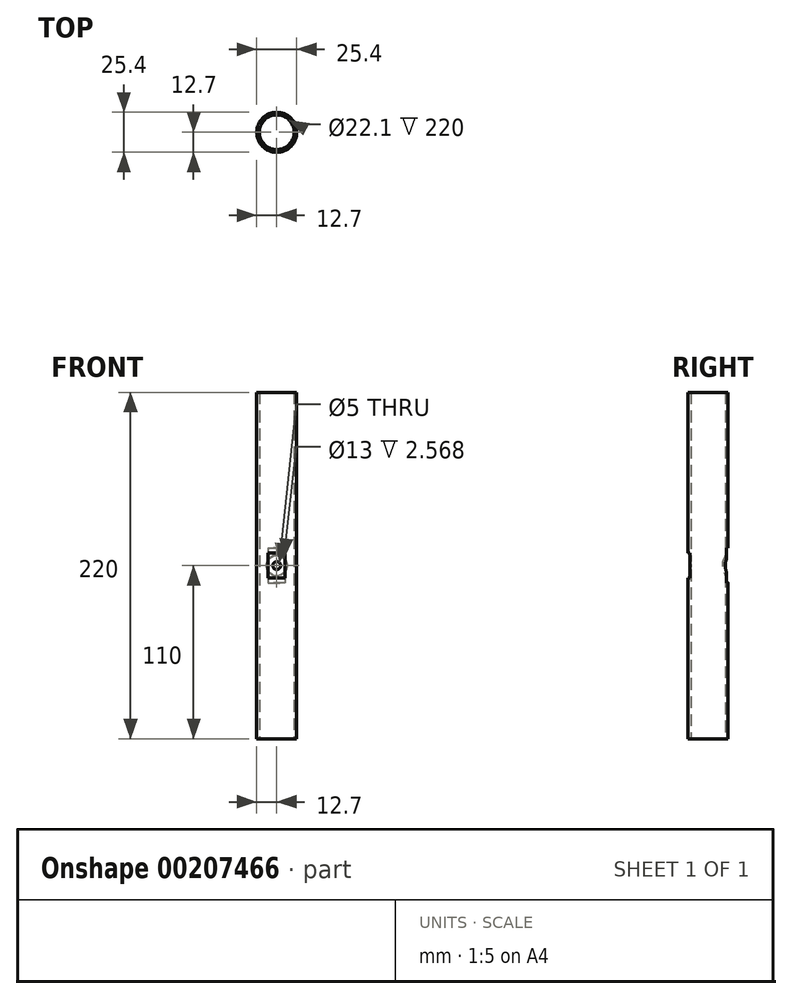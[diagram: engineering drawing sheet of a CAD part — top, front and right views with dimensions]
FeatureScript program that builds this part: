
annotation { "Feature Type Name" : "Feature", "Feature Type Description" : "" }
export const myFeature = defineFeature(function(context is Context, id is Id, definition is map)
    precondition{}
    {
        {
            var Q0;
            Q0=qCreatedBy(makeId("Top.planeOp"),FACE);
            var sketch = newSketch(context, id + "F0", { "sketchPlane" : qUnion([Q0])});
            skCircle(sketch, "E0", {"center": v(0, 0) * mm, "radius": 12.7 * mm});
            skCircle(sketch, "E1", {"center": v(0, 0) * mm, "radius": 11.05 * mm});
            skSolve(sketch);
        }
        {
            var Q0;
            Q0 = qSketchRegion(id + "F0", true);
            extrude(context, id + "F1", {"entities" : qUnion([Q0]), "depth" : 220 * mm});
        }
        {
            var Q0;
            Q0=qCreatedBy(makeId("Top.planeOp"),FACE);
            cPlane(context, id + "F2", {"entities" : qUnion([Q0]), "cplaneType" : CPlaneType.OFFSET, "offset" : (220 / 2) * mm, "width" : 150 * mm, "height" : 150 * mm});
        }
        {
            var Q0;
            Q0=qCreatedBy(makeId("Front.planeOp"),FACE);
            cPlane(context, id + "F3", {"entities" : qUnion([Q0]), "cplaneType" : CPlaneType.OFFSET, "offset" : 25.4 * mm / 2, "width" : 150 * mm, "height" : 150 * mm});
        }
        {
            var Q0;
            Q0=qCreatedBy(makeId("Front.planeOp"),FACE);
            cPlane(context, id + "F4", {"entities" : qUnion([Q0]), "cplaneType" : CPlaneType.OFFSET, "offset" : 25.4 * mm / 2, "oppositeDirection" : true, "width" : 150 * mm, "height" : 150 * mm});
        }
        {
            var Q0;
            Q0=qCreatedBy(id+"F4.planeOp",FACE);
            var sketch = newSketch(context, id + "F5", { "sketchPlane" : qUnion([Q0])});
            skCircle(sketch, "E2", {"center": v(0, 110) * mm, "radius": 6.5 * mm});
            skSolve(sketch);
        }
        {
            var Q0;
            Q0 = qSketchRegion(id + "F5", true);
            extrude(context, id + "F6", {"entities" : qUnion([Q0]), "operationType" : NewBodyOperationType.REMOVE, "depth" : 15 * mm});
        }
        {
            var Q0;
            Q0=qCreatedBy(id+"F4.planeOp",FACE);
            var sketch = newSketch(context, id + "F7", { "sketchPlane" : qUnion([Q0])});
            skLineSegment(sketch, "E3.bottom", {"start": v(17.94, 121) * mm, "end": v(-19.7, 121) * mm});
            skLineSegment(sketch, "E3.top", {"start": v(17.94, 99) * mm, "end": v(-19.7, 99) * mm});
            skLineSegment(sketch, "E3.left", {"start": v(17.94, 121) * mm, "end": v(17.94, 99) * mm});
            skLineSegment(sketch, "E3.right", {"start": v(-19.7, 121) * mm, "end": v(-19.7, 99) * mm});
            skSolve(sketch);
        }
        {
            var Q0;
            Q0 = qSketchRegion(id + "F7", true);
            extrude(context, id + "F8", {"entities" : qUnion([Q0]), "operationType" : NewBodyOperationType.REMOVE, "depth" : 1.2 * mm});
        }
        {
            var Q0;
            Q0=qCreatedBy(id+"F3.planeOp",FACE);
            var sketch = newSketch(context, id + "F9", { "sketchPlane" : qUnion([Q0])});
            skCircle(sketch, "E4", {"center": v(0, 110) * mm, "radius": 2.5 * mm});
            skSolve(sketch);
        }
        {
            var Q0;
            Q0 = qSketchRegion(id + "F9", true);
            extrude(context, id + "F10", {"entities" : qUnion([Q0]), "operationType" : NewBodyOperationType.REMOVE, "oppositeDirection" : true, "depth" : 15 * mm});
        }
        {
            var Q0;
            Q0=qCreatedBy(id+"F3.planeOp",FACE);
            var sketch = newSketch(context, id + "F11", { "sketchPlane" : qUnion([Q0])});
            skLineSegment(sketch, "E5.bottom", {"start": v(-25.94, 118) * mm, "end": v(24.4, 118) * mm});
            skLineSegment(sketch, "E5.top", {"start": v(-25.94, 102) * mm, "end": v(24.4, 102) * mm});
            skLineSegment(sketch, "E5.left", {"start": v(-25.94, 118) * mm, "end": v(-25.94, 102) * mm});
            skLineSegment(sketch, "E5.right", {"start": v(24.4, 118) * mm, "end": v(24.4, 102) * mm});
            skSolve(sketch);
        }
        {
            var Q0;
            Q0 = qSketchRegion(id + "F11", true);
            extrude(context, id + "F12", {"entities" : qUnion([Q0]), "operationType" : NewBodyOperationType.REMOVE, "oppositeDirection" : true, "depth" : 1.2 * mm});
        }
    });
